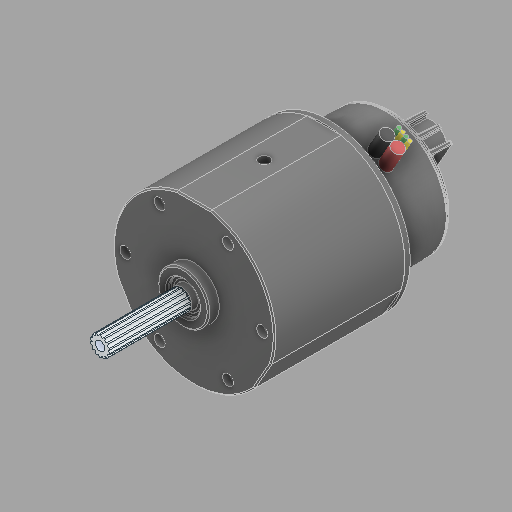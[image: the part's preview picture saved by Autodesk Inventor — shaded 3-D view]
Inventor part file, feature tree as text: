
AUTODESK INVENTOR PART (.ipt)
format: ipt  version: 2024.2 (Build 282272000, 272)  size: 1,163,776 bytes
history: native  units: in
note: dims shown in document units (in); Inventor stores cm internally (conversion verified against a paired STEP export)
features: fillet x4, other x2, chamfer x1
ambient origin geometry x8: Origin, YZ Plane, XZ Plane, XY Plane, X Axis, Y Axis, Z Axis, Center Point
bodies: Solid1 (feature_tree), Solid2 (feature_tree), Solid3 (feature_tree), Solid4 (feature_tree), Solid5 (feature_tree), Solid6 (feature_tree), Solid7 (feature_tree)
feature tree (7):
  chamfer  "Chamfer3"  [1 undecoded]
  other  "Boss-Extrude10"
  fillet  "Fillet4"  [1 undecoded]
  fillet  "Fillet3"  [1 undecoded]
  fillet  "Fillet5"  [1 undecoded]
  fillet  "Fillet6"  [1 undecoded]
  other  "#8-32 Tapped Hole1"
note: 5 required parameter values undecoded (feature->parameter linkage not recoverable at this tier; creation-order binding heuristic only, values carry confidence <= 0.55)
